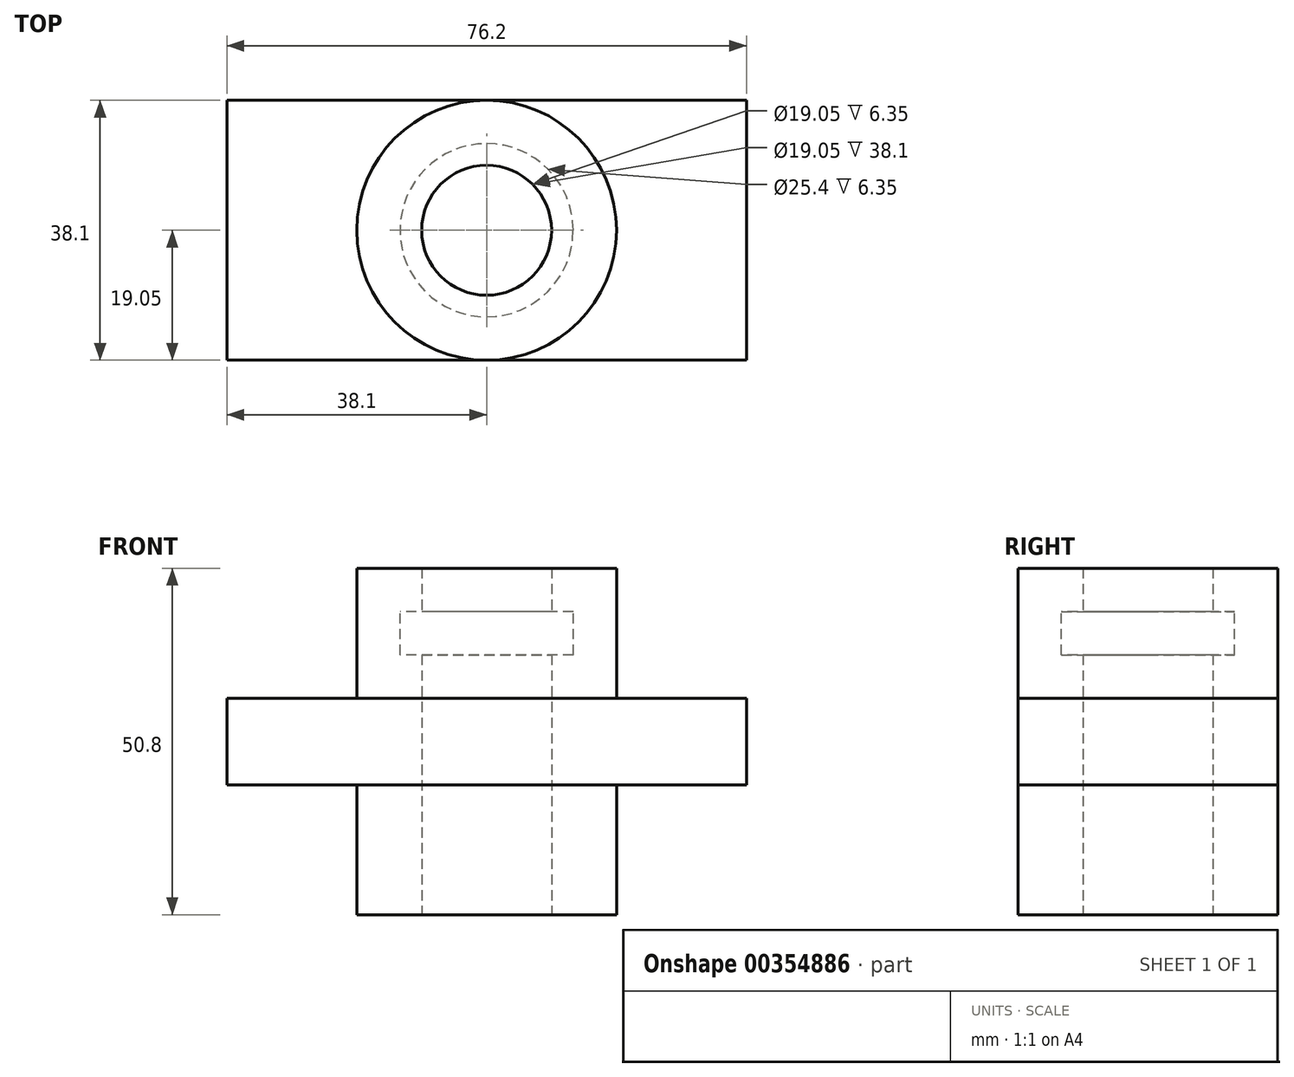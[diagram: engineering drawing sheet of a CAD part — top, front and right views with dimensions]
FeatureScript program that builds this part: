
annotation { "Feature Type Name" : "Feature", "Feature Type Description" : "" }
export const myFeature = defineFeature(function(context is Context, id is Id, definition is map)
    precondition{}
    {
        {
            var Q0;
            Q0=qCreatedBy(makeId("Top.planeOp"),FACE);
            var sketch = newSketch(context, id + "F0", { "sketchPlane" : qUnion([Q0])});
            skCircle(sketch, "E0", {"center": v(0, 0) * mm, "radius": 19.05 * mm});
            skCircle(sketch, "E1", {"center": v(0, 0) * mm, "radius": 9.53 * mm});
            skLineSegment(sketch, "E2", {"start": v(0, 19.05) * mm, "end": v(38.1, 19.05) * mm});
            skLineSegment(sketch, "E3", {"start": v(38.1, 19.05) * mm, "end": v(38.1, -19.05) * mm});
            skLineSegment(sketch, "E4", {"start": v(38.1, -19.05) * mm, "end": v(0, -19.05) * mm});
            skLineSegment(sketch, "E5", {"start": v(0, -19.05) * mm, "end": v(-38.1, -19.05) * mm});
            skLineSegment(sketch, "E6", {"start": v(-38.1, -19.05) * mm, "end": v(-38.1, 19.05) * mm});
            skLineSegment(sketch, "E7", {"start": v(-38.1, 19.05) * mm, "end": v(0, 19.05) * mm});
            skSolve(sketch);
        }
        {
            var Q0;
            Q0=makeQuery(id+"F0.imprint","IMPRINT",FACE,{"disambiguationData":[TD([[makeQuery(id+"F0.imprint","IMPRINT",EDGE,{"derivedFrom":sQuery(id+"F0.wireOp",EDGE,"E1")}),-1.0]])]});
            extrude(context, id + "F1", {"entities" : qUnion([Q0]), "depth" : 25.4 * mm});
        }
        {
            var Q0;
            Q0=makeQuery(id+"F0.imprint","IMPRINT",FACE,{"disambiguationData":[TD([[makeQuery(id+"F0.imprint","IMPRINT",EDGE,{"derivedFrom":sQuery(id+"F0.wireOp",EDGE,"E1")}),-1.0]])]});
            extrude(context, id + "F2", {"entities" : qUnion([Q0]), "operationType" : NewBodyOperationType.ADD, "oppositeDirection" : true, "depth" : 25.4 * mm});
        }
        {
            var Q0;
            {var subQ0=sQuery(id+"F0.wireOp",EDGE,"E2");Q0=makeQuery(id+"F0.imprint","IMPRINT",FACE,{"disambiguationData":[TD([[makeQuery(id+"F0.imprint","IMPRINT",EDGE,{"derivedFrom":subQ0}),-1.0]])]});}
            var Q1;
            {var subQ2=sQuery(id+"F0.wireOp",EDGE,"E5");Q1=makeQuery(id+"F0.imprint","IMPRINT",FACE,{"disambiguationData":[TD([[makeQuery(id+"F0.imprint","IMPRINT",EDGE,{"derivedFrom":subQ2}),-1.0]])]});}
            extrude(context, id + "F3", {"entities" : qUnion([Q0, Q1]), "operationType" : NewBodyOperationType.ADD, "depth" : 12.7 * mm, "symmetric" : true});
        }
        {
            var Q0;
            Q0=qCreatedBy(makeId("Front.planeOp"),FACE);
            var sketch = newSketch(context, id + "F4", { "sketchPlane" : qUnion([Q0])});
            skLineSegment(sketch, "E8", {"start": v(0, 19.05) * mm, "end": v(12.7, 19.05) * mm});
            skLineSegment(sketch, "E9", {"start": v(12.7, 19.05) * mm, "end": v(12.7, 12.7) * mm});
            skLineSegment(sketch, "E10", {"start": v(12.7, 12.7) * mm, "end": v(0, 12.7) * mm});
            skLineSegment(sketch, "E11", {"start": v(0, 12.7) * mm, "end": v(0, 19.05) * mm});
            skSolve(sketch);
        }
        {
            var Q0;
            Q0=makeQuery(id+"F4.imprint","IMPRINT",FACE,{"disambiguationData":[TD([[makeQuery(id+"F4.imprint","IMPRINT",EDGE,{"derivedFrom":sQuery(id+"F4.wireOp",EDGE,"E8")}),-1.0]])]});
            var Q1;
            Q1=sQuery(id+"F4.wireOp",EDGE,"E11");
            revolve(context, id + "F5", {"operationType" : NewBodyOperationType.REMOVE, "entities" : qUnion([Q0]), "axis" : qUnion([Q1]), "revolveType" : RevolveType.FULL, "oppositeDirection" : true});
        }
    });
